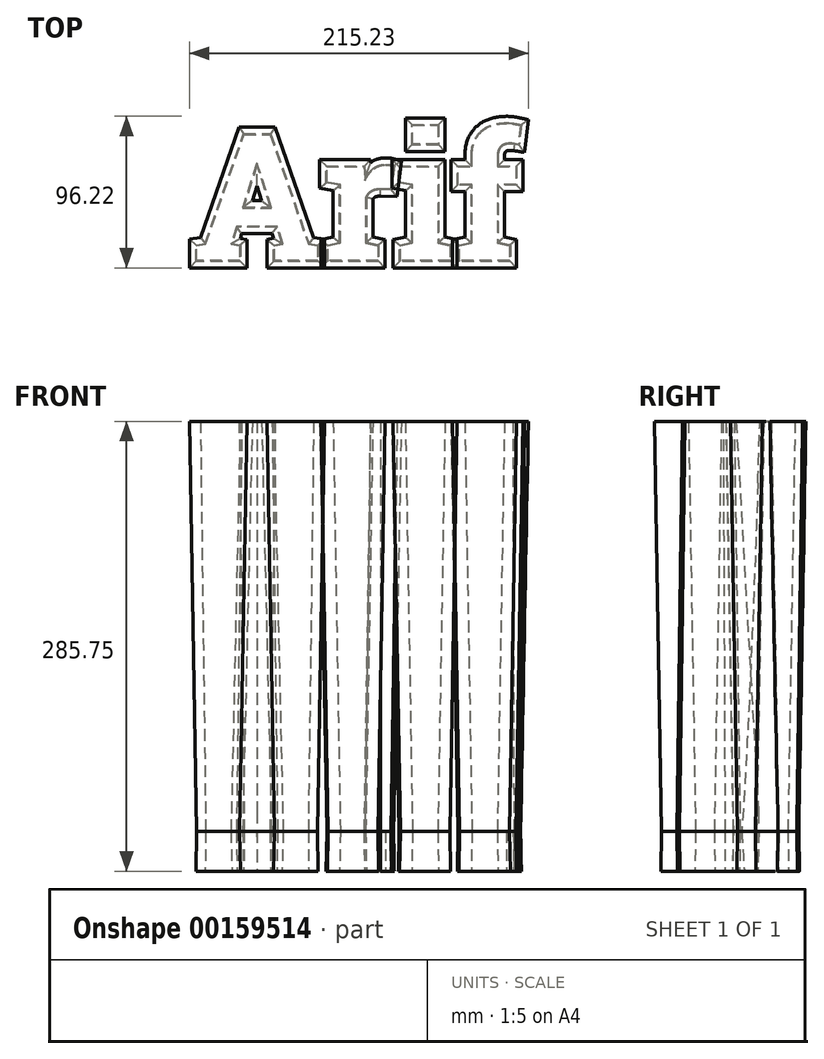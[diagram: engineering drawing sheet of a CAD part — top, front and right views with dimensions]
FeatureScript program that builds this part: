
annotation { "Feature Type Name" : "Feature", "Feature Type Description" : "" }
export const myFeature = defineFeature(function(context is Context, id is Id, definition is map)
    precondition{}
    {
        {
            var Q0;
            Q0=qCreatedBy(makeId("Top.planeOp"),FACE);
            var sketch = newSketch(context, id + "F0", { "sketchPlane" : qUnion([Q0])});
            skText(sketch, "E0", { "text": " Arif", "fontName": "RobotoSlab-Bold.ttf"});
            const initialGuessF0  = {"E0": [-0.01434, -0.0644, 1, 0, 0.08126]};
            skSetInitialGuess(sketch, initialGuessF0);
            skSolve(sketch);
        }
        {
            var Q0;
            Q0 = qSketchRegion(id + "F0", true);
            extrude(context, id + "F1", {"entities" : qUnion([Q0]), "depth" : 260.35 * mm, "hasDraft" : true, "draftAngle" : 1 * degree, "hasSecondDirection" : true, "secondDirectionOppositeDirection" : true, "secondDirectionDepth" : 25.4 * mm, "hasSecondDirectionDraft" : true, "secondDirectionDraftAngle" : 1 * degree});
        }
    });
